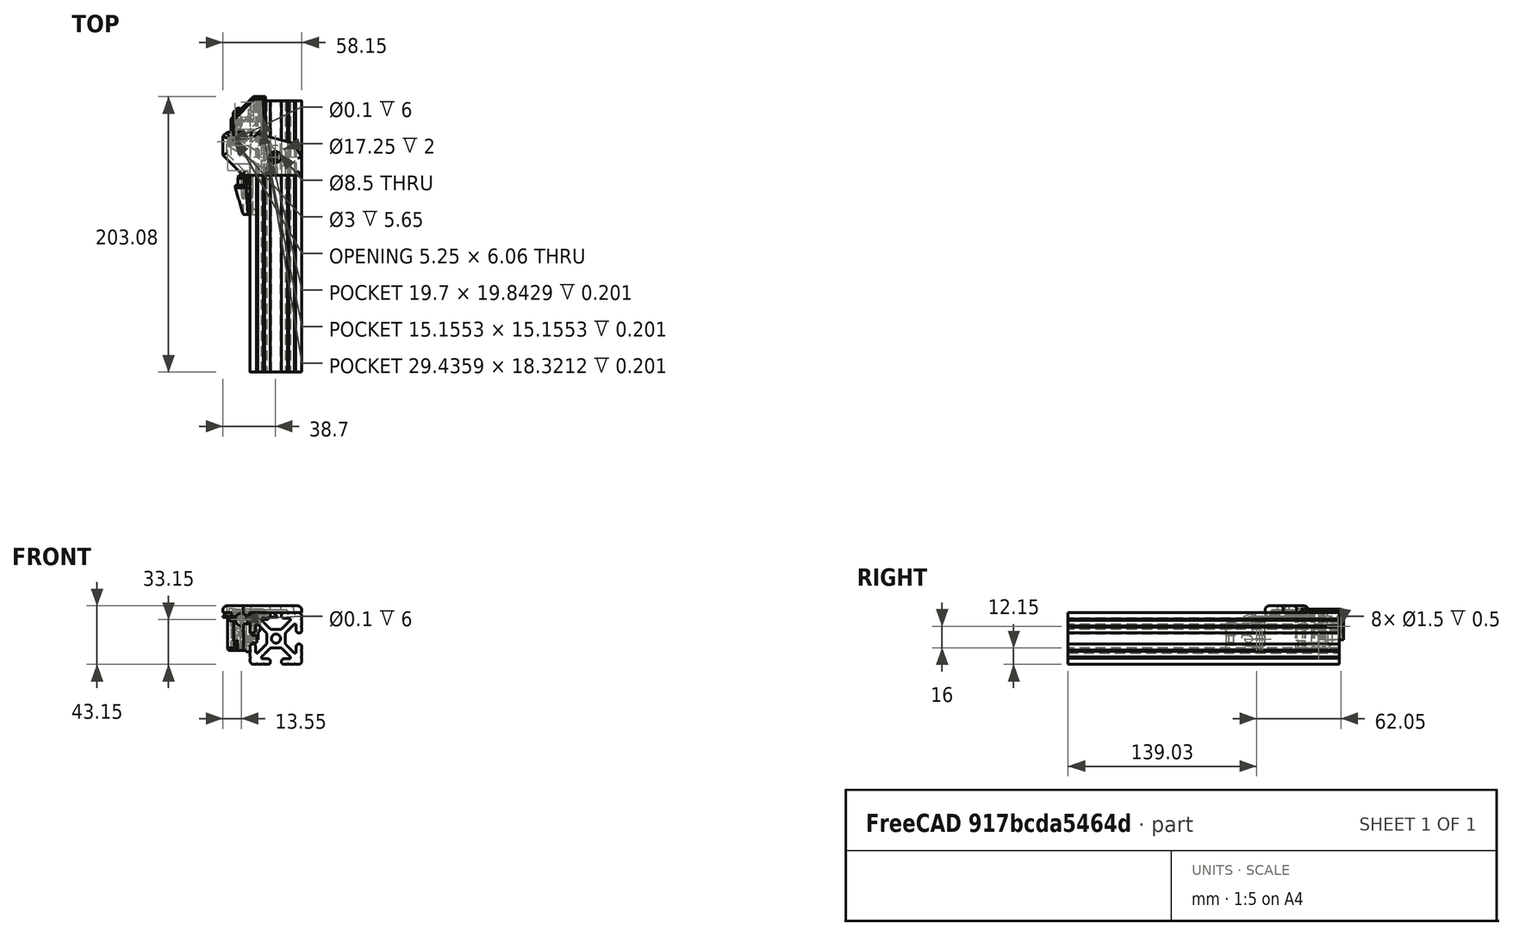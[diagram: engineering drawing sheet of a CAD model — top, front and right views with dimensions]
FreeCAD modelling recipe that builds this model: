
FCSTD DOCUMENT  (FreeCAD 0.18R)
Label: rambo-lower-mount
License: All rights reserved
LicenseURL: http://en.wikipedia.org/wiki/All_rights_reserved
objects: Part::Feature×5, Sketcher::SketchObject×5, PartDesign::Fillet×4, PartDesign::Pad×3, PartDesign::Pocket×2, Mesh::Feature×2, PartDesign::Body×1
note: 25 computed .brp shape members not serialized (recipe doc carries the construction recipe); baked Part::Feature solids carry a one-line shape summary decoded from their .brp

FEATURE [Part::Feature] rambo_base_lower_mount
  shape: bbox 39.91 x 31.71 x 6.307 mm, 79 faces (baked)
FEATURE [Part::Feature] rambo_base_upper_mount
  shape: bbox 25.4 x 33.05 x 22.5 mm, 98 faces (baked)
FEATURE [Part::Feature] rambo_lid_lower_hinge
  Placement = pos=(7.5,-32,-5) rot=(-1,0,0;1.5708rad)
  shape: bbox 15.91 x 29.3 x 28.51 mm, 59 faces (baked)
FEATURE [Part::Feature] rambo_lid_upper_hinge
  shape: bbox 14.19 x 26.95 x 28 mm, 51 faces (baked)
FEATURE [Sketcher::SketchObject] Sketch
  MapMode = 5
  Support = -> [XY_Plane]
  sketch-geometry (9):
    g0: LineSegment StartX=-3 StartY=6.9 StartZ=0 EndX=15 EndY=6.9 EndZ=0
    g1: LineSegment StartX=15 StartY=6.9 StartZ=0 EndX=46.204 EndY=-1.4611 EndZ=0
    g2: LineSegment StartX=52 StartY=-11.5 StartZ=0 EndX=52 EndY=-24.8 EndZ=0
    g3: LineSegment StartX=52 StartY=-24.8 StartZ=0 EndX=8.85 EndY=-24.8 EndZ=0
    g4: LineSegment StartX=8.85 StartY=-24.8 StartZ=0 EndX=-6.05 EndY=-9.9 EndZ=0
    g5: LineSegment StartX=-6.05 StartY=-9.9 StartZ=0 EndX=-6.05 EndY=3.85 EndZ=0
    g6: LineSegment StartX=-6.05 StartY=3.85 StartZ=0 EndX=-3 EndY=6.9 EndZ=0
    g7: LineSegment StartX=46.204 StartY=-1.4611 StartZ=0 EndX=52 EndY=-11.5 EndZ=0
    g8: Circle CenterX=32.65 CenterY=-11.5 CenterZ=0 NormalX=0 NormalY=0 NormalZ=1 AngleXU=0 Radius=4.25
  constraints (27):
    c: Horizontal(g0)
    c: Vertical(g2)
    c: Horizontal(g3)
    c: Vertical(g5)
    c: Coincident(g6,g5)
    c: Coincident(g6,g0)
    c: Coincident(g4,g3)
    c: Coincident(g2,g3)
    c: Coincident(g7,g1)
    c: DistanceY(g-1,g0) = 6.9
    c: Angle(g3,g4) = 2.35619
    c: Coincident(g5,g4)
    c: DistanceX(g-1,g0) = 15
    c: Coincident(g7,g2)
    c: DistanceX(g0,g2) = 37
    c: Angle(g1,g7) = 2.35619
    c: Coincident(g1,g0)
    c: Angle(g7,g2) = 2.61799
    c: Angle(g6,g0) = 2.35619
    c: DistanceX(g5,g-1) = 6.05
    c: DistanceY(g3,g-1) = 24.8
    c: DistanceY(g8,g-1) = 11.5
    c: Diameter(g8) = 8.5
    c: DistanceY(g2,g8) = 0
    c: DistanceY(g4,g-1) = 9.9
    c: DistanceX(g0,g-1) = 3
    c: DistanceX(g-1,g8) = 32.65
FEATURE [PartDesign::Pad] Pad
  Length = 5
  Length2 = 100
  Profile = -> Sketch
  Type = 0
FEATURE [Sketcher::SketchObject] Sketch001
  MapMode = 5
  Support = -> [XY_Plane]
  sketch-geometry (4):
    g0: LineSegment StartX=0.3 StartY=-16.25 StartZ=0 EndX=13.9 EndY=-16.25 EndZ=0
    g1: LineSegment StartX=13.9 StartY=-16.25 StartZ=0 EndX=13.9 EndY=-24.8 EndZ=0
    g2: LineSegment StartX=0.3 StartY=-16.25 StartZ=0 EndX=8.85 EndY=-24.8 EndZ=0
    g3: LineSegment StartX=8.85 StartY=-24.8 StartZ=0 EndX=13.9 EndY=-24.8 EndZ=0
  constraints (12):
    c: Horizontal(g0)
    c: Vertical(g1)
    c: Coincident(g2,g0)
    c: Coincident(g3,g2)
    c: Coincident(g3,g1)
    c: Horizontal(g3)
    c: Coincident(g0,g1)
    c: Angle(g3,g2) = 2.35619
    c: DistanceX(g-1,g0) = 0.3
    c: DistanceX(g-1,g0) = 13.9
    c: DistanceY(g1,g-1) = 24.8
    c: DistanceY(g1,g1) = 8.55
FEATURE [PartDesign::Pad] Pad001
  BaseFeature = -> Pad
  Length = 3
  Length2 = 100
  Profile = -> Sketch001
  Reversed = true
  Type = 0
FEATURE [Sketcher::SketchObject] Sketch002
  MapMode = 5
  Support = -> [XY_Plane]
  sketch-geometry (7):
    g0: LineSegment StartX=0 StartY=-3.05 StartZ=0 EndX=2.64138 EndY=-1.525 EndZ=0
    g1: LineSegment StartX=2.64138 StartY=-1.525 StartZ=0 EndX=2.64138 EndY=1.525 EndZ=0
    g2: LineSegment StartX=2.64138 StartY=1.525 StartZ=0 EndX=4e-16 EndY=3.05 EndZ=0
    g3: LineSegment StartX=4e-16 StartY=3.05 StartZ=0 EndX=-2.64138 EndY=1.525 EndZ=0
    g4: LineSegment StartX=-2.64138 StartY=1.525 StartZ=0 EndX=-2.64138 EndY=-1.525 EndZ=0
    g5: LineSegment StartX=-2.64138 StartY=-1.525 StartZ=0 EndX=0 EndY=-3.05 EndZ=0
    g6: Circle [constr] CenterX=0 CenterY=0 CenterZ=0 NormalX=0 NormalY=0 NormalZ=1 AngleXU=0 Radius=3.05
  constraints (16):
    c: Coincident(g0,g1)
    c: Coincident(g1,g2)
    c: Coincident(g2,g3)
    c: Coincident(g3,g4)
    c: Coincident(g4,g5)
    c: Coincident(g5,g0)
    c: Equal(g0, g1-g5) x5
    c: PointOnObject(g0,g6)
    c: PointOnObject(g1,g6)
    c: PointOnObject(g2,g6)
    c: PointOnObject(g3,g6)
    c: PointOnObject(g4,g6)
    c: PointOnObject(g5,g6)
    c: Coincident(g6,g-1)
    c: PointOnObject(g5,g-2)
    c: DistanceY(g-1,g2) = 3.05
FEATURE [PartDesign::Pad] Pad002
  BaseFeature = -> Pad001
  Length = 3
  Length2 = 100
  Profile = -> Sketch002
  Reversed = true
  Type = 0
FEATURE [Sketcher::SketchObject] Sketch003
  AttachmentOffset = pos=(0,0,-3) rot=(0,0,1;0rad)
  MapMode = 5
  Placement = pos=(0,0,-3) rot=(0,0,1;0rad)
  Support = -> [XY_Plane]
  sketch-geometry (1):
    g0: Circle CenterX=0 CenterY=0 CenterZ=0 NormalX=0 NormalY=0 NormalZ=1 AngleXU=0 Radius=1.5
  constraints (2):
    c: Diameter(g0) = 3
    c: Coincident(g0,g-1)
FEATURE [PartDesign::Pocket] Pocket
  BaseFeature = -> Pad002
  Length = 6
  Length2 = 100
  Profile = -> Sketch003
  Reversed = true
  Type = 0
FEATURE [Sketcher::SketchObject] Sketch004
  AttachmentOffset = pos=(0,0,2) rot=(0,0,1;0rad)
  MapMode = 5
  Placement = pos=(0,0,2) rot=(0,0,1;0rad)
  Support = -> [XY_Plane]
  sketch-geometry (1):
    g0: Circle CenterX=32.65 CenterY=-11.5 CenterZ=0 NormalX=0 NormalY=0 NormalZ=1 AngleXU=0 Radius=8.625
  constraints (3):
    c: DistanceX(g-1,g0) = 32.65
    c: DistanceY(g0,g-1) = 11.5
    c: Diameter(g0) = 17.25
FEATURE [PartDesign::Pocket] Pocket001
  BaseFeature = -> Pocket
  Length = 6
  Length2 = 100
  Profile = -> Sketch004
  Type = 0
FEATURE [PartDesign::Fillet] Fillet
  Base = -> Pocket001 [Edge50,Edge48,Edge46,Edge55,Edge54,Edge52]
  BaseFeature = -> Pocket001
  Radius = 0.25
FEATURE [PartDesign::Fillet] Fillet001
  Base = -> Fillet [Edge36]
  BaseFeature = -> Fillet
  Radius = 0.35
FEATURE [PartDesign::Fillet] Fillet002
  Base = -> Fillet001 [Edge75,Edge65,Edge61,Edge74]
  BaseFeature = -> Fillet001
  Radius = 1
FEATURE [PartDesign::Fillet] Fillet003
  Base = -> Fillet002 [Edge51,Edge33,Edge42,Edge41,Edge44,Edge46,Edge48,Edge50]
  BaseFeature = -> Fillet002
  Radius = 3
FEATURE [PartDesign::Body] Body  label="rambo-lower-mount"
  Group = -> [Sketch,Pad,Sketch001,Pad001,Sketch002,Pad002,Sketch003,Pocket,Sketch004,Pocket001,Fillet,Fillet001,Fillet002,Fillet003]
  Origin = -> Origin
  Tip = -> Fillet003
FEATURE [Part::Feature] _515_extrusion_200_25mm_7_7_8in
  Placement = pos=(-113,30,-76.25) rot=(1,0,0;1.5708rad)
  shape: bbox 38.1 x 200 x 38.1 mm, 113 faces (baked)
FEATURE [Mesh::Feature] Einsy_base  label="Einsy-base"
  Placement = pos=(54,0,-5.6e-15) rot=(0.57735,0.57735,-0.57735;4.18879rad)
FEATURE [Mesh::Feature] Einsy_doors  label="Einsy-doors"
  Placement = pos=(3,73.5,82.5) rot=(0.57735,-0.57735,0.57735;4.18879rad)
